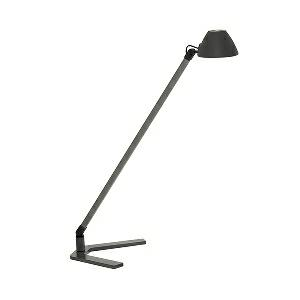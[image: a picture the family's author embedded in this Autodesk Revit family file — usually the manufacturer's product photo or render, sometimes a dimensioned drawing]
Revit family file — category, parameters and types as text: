
# Revit family: lucio_-_lum_500_830_d_00804140_9e7a
name_source: partatom
category: Lighting Fixtures
units: mm (PartAtom-declared; Revit-internal decimal feet)

## family parameters
Cut with Voids When Loaded = No
Host = Face
Light Source = No
Part Type = Normal
Room Calculation Point = No
Round Connector Dimension = Use Diameter
Shared = No

## types (1)
- LUCIO - LUM 500/830/D (1 x LED, 265 lm, 3000K)
    Apparent Load = 4 VA
    Approval mark = CE
    CIE Flux Codes = 84 97 99 100 100
    Color Rendering = 80-89
    Color Temperature = 3000K
    Control Gear = Electronic ballast
    Default Elevation = 1800 mm
    Description = LUM 500/830/D|Task luminaire|light source: LED module|work equipment: Electronic plug-in transformer|connected load: 100-240 V, 50/60 Hz|Power consumption: approx. 4 W|standby: approx. 0,30|power factor: approx. 0,970|luminous flux: 265 lm|luminous efficacy: 66 lm/W|Illuminance efficiency factor: 0 lx/W|colour temperature: Warm white, ca. 3000 K|color rendering index (CRI): >= 80|chromaticity tolerance:  3 SDCM|class of protection: II with plug-in power supply, III without plug-in power supply|technology: Continuously dimmable|luminaire body|material: Plastic|surface: Untreated|colour: Umbra grey|lamp cover: Polycarbonate (PC), Satine|tubular sections|material: Tubular aluminium section|surface: Anodized|Form: Tubular section upright|colour: Titanium|weight (net): approx. 1.0 kg|mains lead: 1.85 m Mains plug CEE 7/XVI|Fastening: Adaptor (accessory), Table base, Table clamp (accessory)|glare control: Optics|special features: Push button in luminaire head|Approval mark: VDE - ENEC|
    Frequency = 50 Hz
    Height = 55 mm
    Lamp = 1 x LED
    Lamp Light Flux = 265 lm
    Lamp count = 1
    Length = 90 mm
    Luminous efficacy = 66 lm/W
    Manufacturer = Waldmann
    ModVariant = No
    Model = 00804140
    Mounting Place = Table
    Mounting Type = Surface mounted
    Number of Poles = 1
    OnlyDefault = Yes
    Power Factor = 1
    Product Name = LUCIO - LUM 500/830/D
    Product group = Task luminaire (office)
    ProductGroupID = 21
    Protection Class = Protection class II
    Protection Degree = IP 20
    RLX_Detail_Level = 1
    RLX_Emergency_Light_Flux = 0 lm
    RLX_Emergency_Type = 0
    RLX_Emergency_Type_DB = No
    RlxData = <blob elided: 63317 chars, md5=e1a091c5>
    Socket = socket
    Standby Power = 0 W
    System Light Flux = 265 lm
    System Power = 4 W
    Type Comments = Product without accessories
    Type Image = 00804142.jpg
    URL = http://relux.com
    VarID = ---
    Voltage = 230 V
    Voltage Range = 220-240 V
    Weight = 0.00 kg
    Width = 0 mm  [stored 0 ft]

note: [stored X ft] marks values corroborated as IEEE doubles in the binary element streams (Revit-internal decimal feet)

## geometry (parser evidence)
native form markers: Blend x4, Sweep x15
no freeform markers — native parametric forms only
